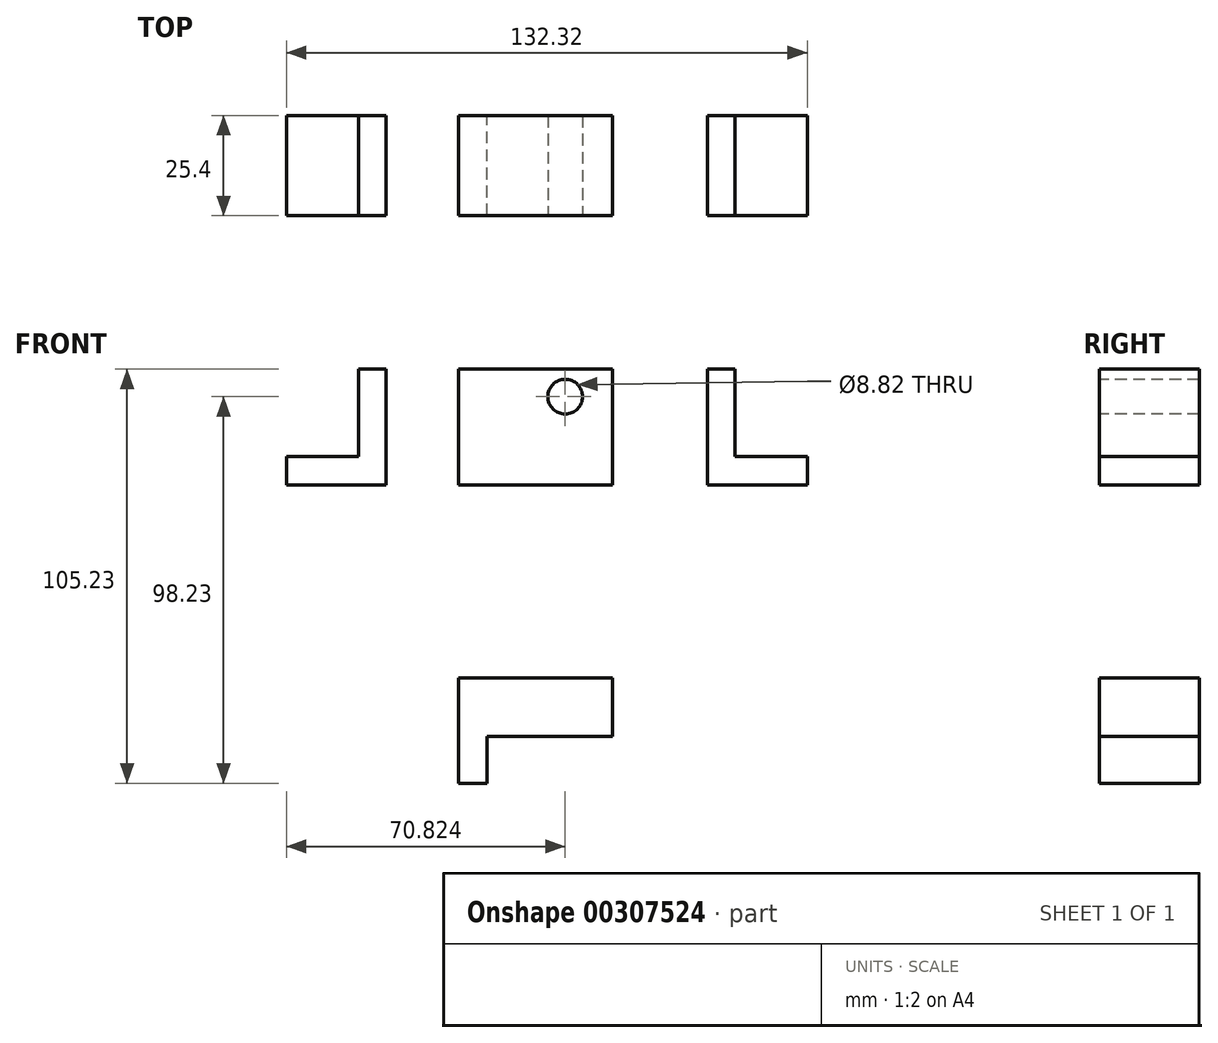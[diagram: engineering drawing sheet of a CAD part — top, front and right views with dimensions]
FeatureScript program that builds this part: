
annotation { "Feature Type Name" : "Feature", "Feature Type Description" : "" }
export const myFeature = defineFeature(function(context is Context, id is Id, definition is map)
    precondition{}
    {
        {
            var Q0;
            Q0=qCreatedBy(makeId("Front.planeOp"),FACE);
            var sketch = newSketch(context, id + "F0", { "sketchPlane" : qUnion([Q0])});
            skLineSegment(sketch, "E0", {"start": v(-22.44, 53.49) * mm, "end": v(16.61, 53.49) * mm});
            skLineSegment(sketch, "E1", {"start": v(16.61, 53.49) * mm, "end": v(16.61, 24.05) * mm});
            skLineSegment(sketch, "E2", {"start": v(16.61, 24.05) * mm, "end": v(-22.44, 24.05) * mm});
            skLineSegment(sketch, "E3", {"start": v(-22.44, 24.05) * mm, "end": v(-22.44, 53.49) * mm});
            skLineSegment(sketch, "E4", {"start": v(40.8, 53.49) * mm, "end": v(40.8, 24.05) * mm});
            skLineSegment(sketch, "E5", {"start": v(40.8, 24.05) * mm, "end": v(66.16, 24.05) * mm});
            skLineSegment(sketch, "E6", {"start": v(66.16, 24.05) * mm, "end": v(66.16, 31.33) * mm});
            skLineSegment(sketch, "E7", {"start": v(66.16, 31.33) * mm, "end": v(47.8, 31.33) * mm});
            skLineSegment(sketch, "E8", {"start": v(47.8, 31.33) * mm, "end": v(47.8, 53.49) * mm});
            skLineSegment(sketch, "E9", {"start": v(47.8, 53.49) * mm, "end": v(40.8, 53.49) * mm});
            skLineSegment(sketch, "E10.MirrorCS", {"start": v(-47.8, 53.49) * mm, "end": v(-40.8, 53.49) * mm});
            skLineSegment(sketch, "E11.MirrorCS", {"start": v(-66.16, 24.05) * mm, "end": v(-66.16, 31.33) * mm});
            skLineSegment(sketch, "E12.MirrorCS", {"start": v(-47.8, 31.33) * mm, "end": v(-47.8, 53.49) * mm});
            skLineSegment(sketch, "E13.MirrorCS", {"start": v(-40.8, 53.49) * mm, "end": v(-40.8, 24.05) * mm});
            skLineSegment(sketch, "E14.MirrorCS", {"start": v(-66.16, 31.33) * mm, "end": v(-47.8, 31.33) * mm});
            skLineSegment(sketch, "E15.MirrorCS", {"start": v(-40.8, 24.05) * mm, "end": v(-66.16, 24.05) * mm});
            skLineSegment(sketch, "E16", {"start": v(-22.44, -24.92) * mm, "end": v(16.61, -24.92) * mm});
            skLineSegment(sketch, "E17", {"start": v(16.61, -24.92) * mm, "end": v(16.61, -39.79) * mm});
            skLineSegment(sketch, "E18", {"start": v(-22.44, -24.92) * mm, "end": v(-22.44, -51.74) * mm});
            skLineSegment(sketch, "E19", {"start": v(-22.44, -51.74) * mm, "end": v(-15.16, -51.74) * mm});
            skLineSegment(sketch, "E20", {"start": v(-15.16, -51.74) * mm, "end": v(-15.16, -39.79) * mm});
            skLineSegment(sketch, "E21", {"start": v(-15.16, -39.79) * mm, "end": v(16.61, -39.79) * mm});
            skSolve(sketch);
        }
        {
            var Q0;
            Q0 = qSketchRegion(id + "F0", true);
            extrude(context, id + "F1", {"entities" : qUnion([Q0]), "depth" : 25.4 * mm});
        }
        {
            var Q0;
            Q0=makeQuery(id+"F1.opExtrude","CAP_FACE",FACE,{"disambiguationData":[OSD([sQuery(id+"F0.wireOp",EDGE,"E0"),sQuery(id+"F0.wireOp",EDGE,"E1"),sQuery(id+"F0.wireOp",EDGE,"E2"),sQuery(id+"F0.wireOp",EDGE,"E3")])],"isStart":false});
            var sketch = newSketch(context, id + "F2", { "sketchPlane" : qUnion([Q0])});
            skCircle(sketch, "E22", {"center": v(4.66, 46.5) * mm, "radius": 4.41 * mm});
            skSolve(sketch);
        }
        {
            var Q0;
            Q0 = qSketchRegion(id + "F2", true);
            extrude(context, id + "F3", {"entities" : qUnion([Q0]), "operationType" : NewBodyOperationType.REMOVE, "oppositeDirection" : true, "depth" : 25.4 * mm});
        }
    });
